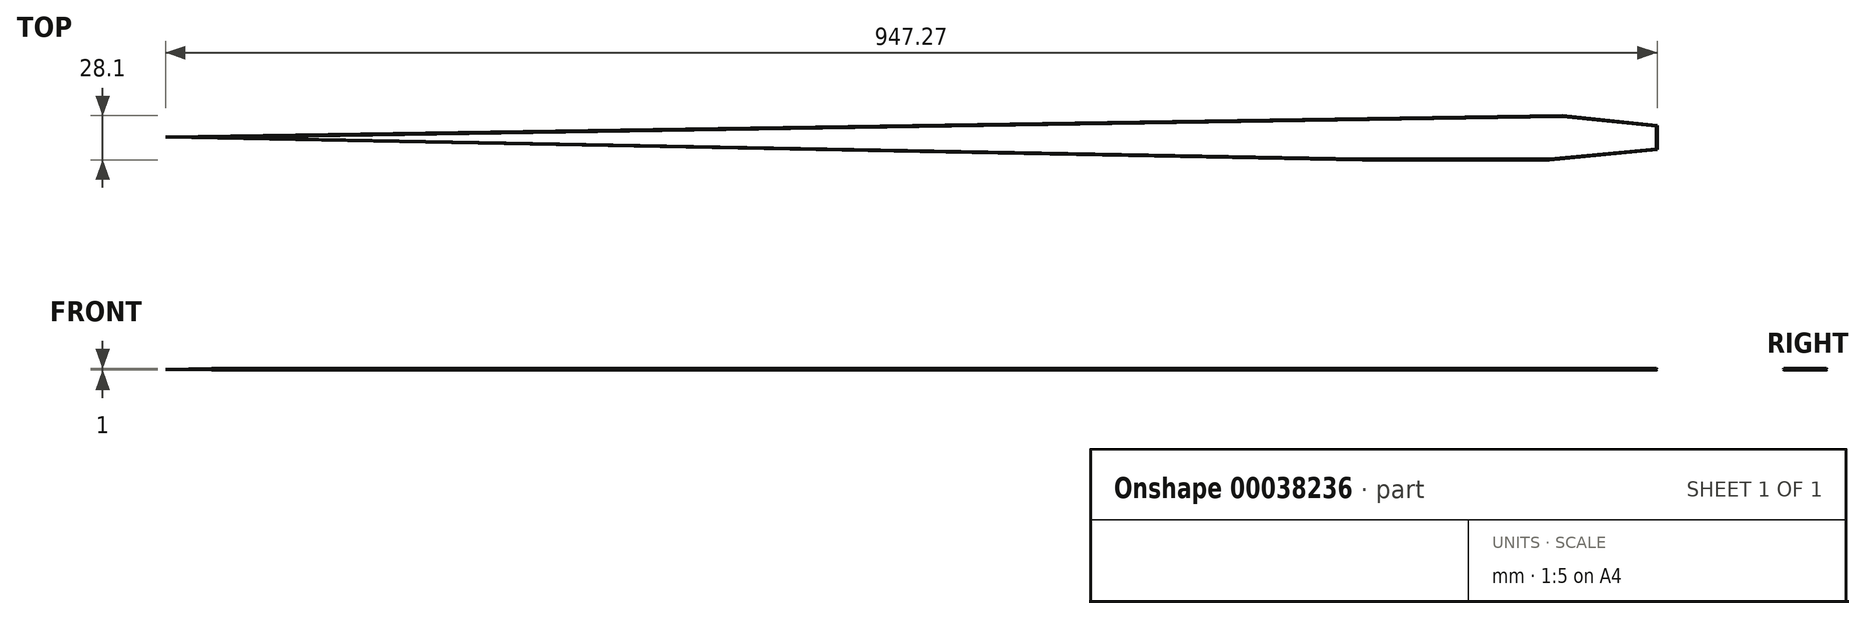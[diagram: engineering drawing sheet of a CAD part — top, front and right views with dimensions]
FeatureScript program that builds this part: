
annotation { "Feature Type Name" : "Feature", "Feature Type Description" : "" }
export const myFeature = defineFeature(function(context is Context, id is Id, definition is map)
    precondition{}
    {
        {
            var Q0;
            Q0=qCreatedBy(makeId("Top.planeOp"),FACE);
            var sketch = newSketch(context, id + "F0", { "sketchPlane" : qUnion([Q0])});
            skLineSegment(sketch, "E0", {"start": v(-53.1, -1.05) * mm, "end": v(888.95, 13.42) * mm});
            skLineSegment(sketch, "E1.top", {"start": v(-53.1, -15.52) * mm, "end": v(894.17, -15.52) * mm});
            skLineSegment(sketch, "E2", {"start": v(-53.1, -1.05) * mm, "end": v(707.09, -15.52) * mm});
            skLineSegment(sketch, "E1.bottom", {"start": v(-53.1, 13.42) * mm, "end": v(894.17, 13.42) * mm});
            skLineSegment(sketch, "E1.right", {"start": v(894.17, 13.42) * mm, "end": v(894.17, -15.52) * mm});
            skLineSegment(sketch, "E1.left", {"start": v(-53.1, 13.42) * mm, "end": v(-53.1, -15.52) * mm});
            skLineSegment(sketch, "E3", {"start": v(825.8, -15.52) * mm, "end": v(894.17, -8.98) * mm});
            skLineSegment(sketch, "E4", {"start": v(894.17, -8.98) * mm, "end": v(825.8, -15.52) * mm});
            skLineSegment(sketch, "E5", {"start": v(894.17, 6.37) * mm, "end": v(825.69, 13.42) * mm});
            skSolve(sketch);
        }
        {
            var Q0;
            {var subQ3=sQuery(id+"F0.wireOp",EDGE,"b5feb1f4-c6b9-4b5a-88b9-fd450c246ee5.right");Q0=makeQuery(id+"F0.imprint","IMPRINT",FACE,{"disambiguationData":[TD([[makeQuery(id+"F0.imprint","IMPRINT",EDGE,{"derivedFrom":subQ3}),-1.0]])]});}
            var Q1;
            {var subQ6=sQuery(id+"F0.wireOp",EDGE,"E2");Q1=makeQuery(id+"F0.imprint","IMPRINT",FACE,{"disambiguationData":[TD([[makeQuery(id+"F0.imprint","IMPRINT",EDGE,{"derivedFrom":subQ6}),1.0]])]});}
            extrude(context, id + "F1", {"entities" : qUnion([Q0, Q1]), "depth" : 1 * mm});
        }
        {
            var Q0;
            Q0=makeQuery(id+"F1.opExtrude","CAP_FACE",FACE,{"disambiguationData":[OSD([sQuery(id+"F0.wireOp",EDGE,"b5feb1f4-c6b9-4b5a-88b9-fd450c246ee5.bottom"),sQuery(id+"F0.wireOp",EDGE,"b5feb1f4-c6b9-4b5a-88b9-fd450c246ee5.top"),sQuery(id+"F0.wireOp",EDGE,"b5feb1f4-c6b9-4b5a-88b9-fd450c246ee5.right"),sQuery(id+"F0.wireOp",EDGE,"2ee9e50e-640c-4978-8cb5-9399d8affe9a"),sQuery(id+"F0.wireOp",EDGE,"ed85e29b-7856-4298-a567-f1f263238bf6")])],"isStart":false});
            var Q1;
            Q1=makeQuery(id+"F1.opExtrude","CAP_FACE",FACE,{"disambiguationData":[OSD([sQuery(id+"F0.wireOp",EDGE,"E0"),sQuery(id+"F0.wireOp",EDGE,"E1.top"),sQuery(id+"F0.wireOp",EDGE,"E2"),sQuery(id+"F0.wireOp",EDGE,"E1.bottom"),sQuery(id+"F0.wireOp",EDGE,"E1.right")])],"isStart":false});
            chamfer(context, id + "F2", {"entities" : qUnion([Q0, Q1]), "width" : 0.5 * mm, "tangentPropagation" : true});
        }
        {
            var Q0;
            Q0=makeQuery(id+"F1.opExtrude","CAP_FACE",FACE,{"disambiguationData":[OSD([sQuery(id+"F0.wireOp",EDGE,"E0"),sQuery(id+"F0.wireOp",EDGE,"E1.top"),sQuery(id+"F0.wireOp",EDGE,"E2"),sQuery(id+"F0.wireOp",EDGE,"E1.bottom"),sQuery(id+"F0.wireOp",EDGE,"E1.right")])],"isStart":true});
            chamfer(context, id + "F3", {"entities" : qUnion([Q0]), "width" : 0.5 * mm, "tangentPropagation" : true});
        }
    });
